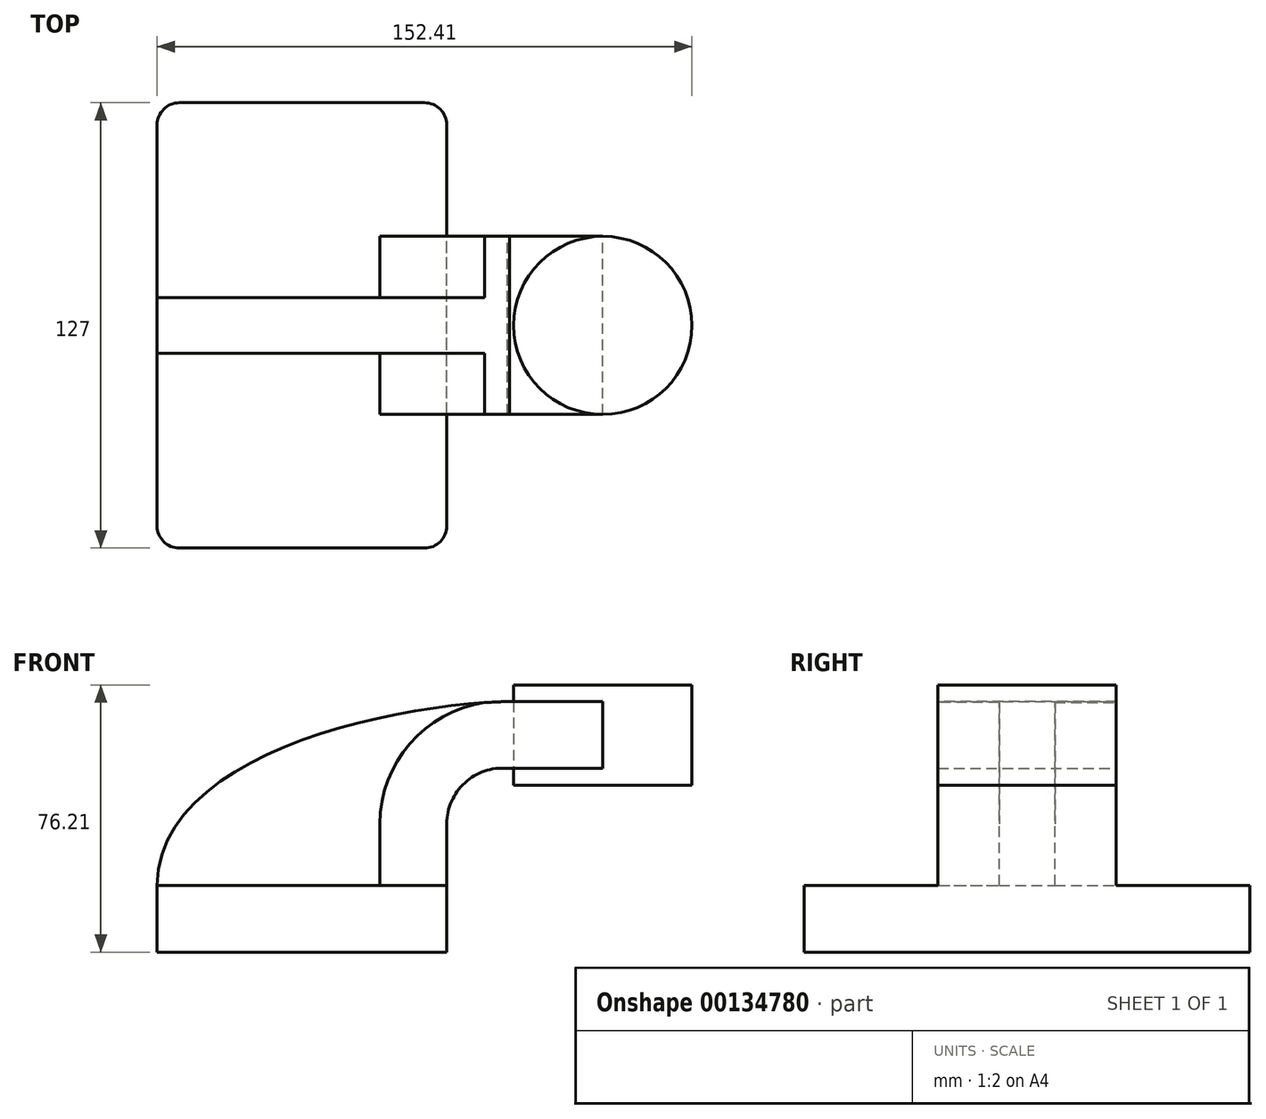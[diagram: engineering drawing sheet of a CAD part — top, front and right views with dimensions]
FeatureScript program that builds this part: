
annotation { "Feature Type Name" : "Feature", "Feature Type Description" : "" }
export const myFeature = defineFeature(function(context is Context, id is Id, definition is map)
    precondition{}
    {
        {
            var Q0;
            Q0=qCreatedBy(makeId("Front.planeOp"),FACE);
            var sketch = newSketch(context, id + "F0", { "sketchPlane" : qUnion([Q0])});
            skLineSegment(sketch, "E0.bottom", {"start": v(-41.28, -9.53) * mm, "end": v(41.28, -9.53) * mm});
            skLineSegment(sketch, "E0.top", {"start": v(-41.28, 9.53) * mm, "end": v(41.28, 9.53) * mm});
            skLineSegment(sketch, "E0.left", {"start": v(-41.28, -9.53) * mm, "end": v(-41.28, 9.53) * mm});
            skLineSegment(sketch, "E0.right", {"start": v(41.28, -9.53) * mm, "end": v(41.28, 9.53) * mm});
            skPoint(sketch, "E0.middle", {"position": v(0, 0) * mm});
            skLineSegment(sketch, "E1.bottom", {"start": v(60.32, 38.1) * mm, "end": v(111.12, 38.1) * mm});
            skLineSegment(sketch, "E1.top", {"start": v(60.32, 66.67) * mm, "end": v(111.12, 66.67) * mm});
            skLineSegment(sketch, "E1.left", {"start": v(60.32, 38.1) * mm, "end": v(60.32, 66.67) * mm});
            skLineSegment(sketch, "E1.right", {"start": v(111.12, 38.1) * mm, "end": v(111.12, 66.67) * mm});
            skPoint(sketch, "E1.middle", {"position": v(85.72, 52.39) * mm});
            skLineSegment(sketch, "E2", {"start": v(41.28, 9.52) * mm, "end": v(41.28, 27.06) * mm});
            skArc(sketch, "E3", {"start": v(41.27, 27.06) * mm, "mid": v(46.4, 38.74) * mm, "end": v(58.47, 42.88) * mm});
            skLineSegment(sketch, "E4", {"start": v(58.47, 42.88) * mm, "end": v(85.72, 42.88) * mm});
            skLineSegment(sketch, "E5.0", {"start": v(59.11, 61.93) * mm, "end": v(85.72, 61.93) * mm});
            skArc(sketch, "E5.1", {"start": v(22.22, 27.06) * mm, "mid": v(33.16, 52.44) * mm, "end": v(59.11, 61.93) * mm});
            skLineSegment(sketch, "E5.2", {"start": v(22.22, 9.52) * mm, "end": v(22.22, 27.06) * mm});
            skLineSegment(sketch, "E6", {"start": v(85.72, 38.1) * mm, "end": v(85.72, 66.67) * mm});
            skFitSpline(sketch, "E7", {"points": [v(-41.28, 9.52) * mm, v(59.11, 61.93) * mm], "startDerivative": vector(1.32, 113.14) * mm, "endDerivative": vector(100.05, 2.04) * mm});
            skSolve(sketch);
        }
        {
            var Q0;
            Q0=makeQuery(id+"F0.imprint","IMPRINT",FACE,{"disambiguationData":[TD([[makeQuery(id+"F0.imprint","IMPRINT",EDGE,{"derivedFrom":sQuery(id+"F0.wireOp",EDGE,"E0.bottom")}),1.0]])]});
            extrude(context, id + "F1", {"entities" : qUnion([Q0]), "endBound" : BoundingType.SYMMETRIC, "depth" : 127 * mm});
        }
        {
            var Q0;
            {var subQ0=sQuery(id+"F0.wireOp",EDGE,"E4");var subQ1=sQuery(id+"F0.wireOp",EDGE,"E1.left");var subQ2=makeQuery(id+"F0.imprint","INTERSECT",VERTEX,{"derivedFrom":[subQ1,subQ0]});Q0=makeQuery(id+"F0.imprint","IMPRINT",FACE,{"disambiguationData":[TD([[makeQuery(id+"F0.imprint","IMPRINT",EDGE,{"disambiguationData":[TD([[subQ2,-1.0]])],"derivedFrom":subQ1}),-1.0]])]});}
            var Q1;
            {var subQ1=sQuery(id+"F0.wireOp",EDGE,"E2");Q1=makeQuery(id+"F0.imprint","IMPRINT",FACE,{"disambiguationData":[TD([[makeQuery(id+"F0.imprint","IMPRINT",EDGE,{"derivedFrom":subQ1}),1.0]])]});}
            extrude(context, id + "F2", {"entities" : qUnion([Q0, Q1]), "operationType" : NewBodyOperationType.ADD, "endBound" : BoundingType.SYMMETRIC, "depth" : 50.8 * mm});
        }
        {
            var Q0;
            {var subQ3=sQuery(id+"F0.wireOp",EDGE,"E5.2");Q0=makeQuery(id+"F0.imprint","IMPRINT",FACE,{"disambiguationData":[TD([[makeQuery(id+"F0.imprint","IMPRINT",EDGE,{"derivedFrom":subQ3}),1.0]])]});}
            extrude(context, id + "F3", {"entities" : qUnion([Q0]), "operationType" : NewBodyOperationType.ADD, "endBound" : BoundingType.SYMMETRIC, "depth" : 15.88 * mm});
        }
        {
            var Q0;
            {var subQ0=sQuery(id+"F0.wireOp",EDGE,"E1.right");Q0=makeQuery(id+"F0.imprint","IMPRINT",FACE,{"disambiguationData":[TD([[makeQuery(id+"F0.imprint","IMPRINT",EDGE,{"derivedFrom":subQ0}),1.0]])]});}
            var Q1;
            Q1=sQuery(id+"F0.wireOp",EDGE,"E6");
            revolve(context, id + "F4", {"entities" : qUnion([Q0]), "axis" : qUnion([Q1]), "revolveType" : RevolveType.FULL});
        }
        {
            var Q0;
            Q0=makeQuery(id+"F1.opExtrude","CAP_EDGE",EDGE,{"disambiguationData":[OSD([sQuery(id+"F0.wireOp",EDGE,"E0.right")])],"isStart":false});
            var Q1;
            Q1=makeQuery(id+"F1.opExtrude","CAP_EDGE",EDGE,{"disambiguationData":[OSD([sQuery(id+"F0.wireOp",EDGE,"E0.left")])],"isStart":false});
            var Q2;
            Q2=makeQuery(id+"F1.opExtrude","CAP_EDGE",EDGE,{"disambiguationData":[OSD([sQuery(id+"F0.wireOp",EDGE,"E0.right")])],"isStart":true});
            var Q3;
            Q3=makeQuery(id+"F1.opExtrude","CAP_EDGE",EDGE,{"disambiguationData":[OSD([sQuery(id+"F0.wireOp",EDGE,"E0.left")])],"isStart":true});
            fillet(context, id + "F5", {"entities" : qUnion([Q0, Q1, Q2, Q3]), "radius" : 6.35 * mm, "tangentPropagation" : true, "allowEdgeOverflow" : false});
        }
    });
